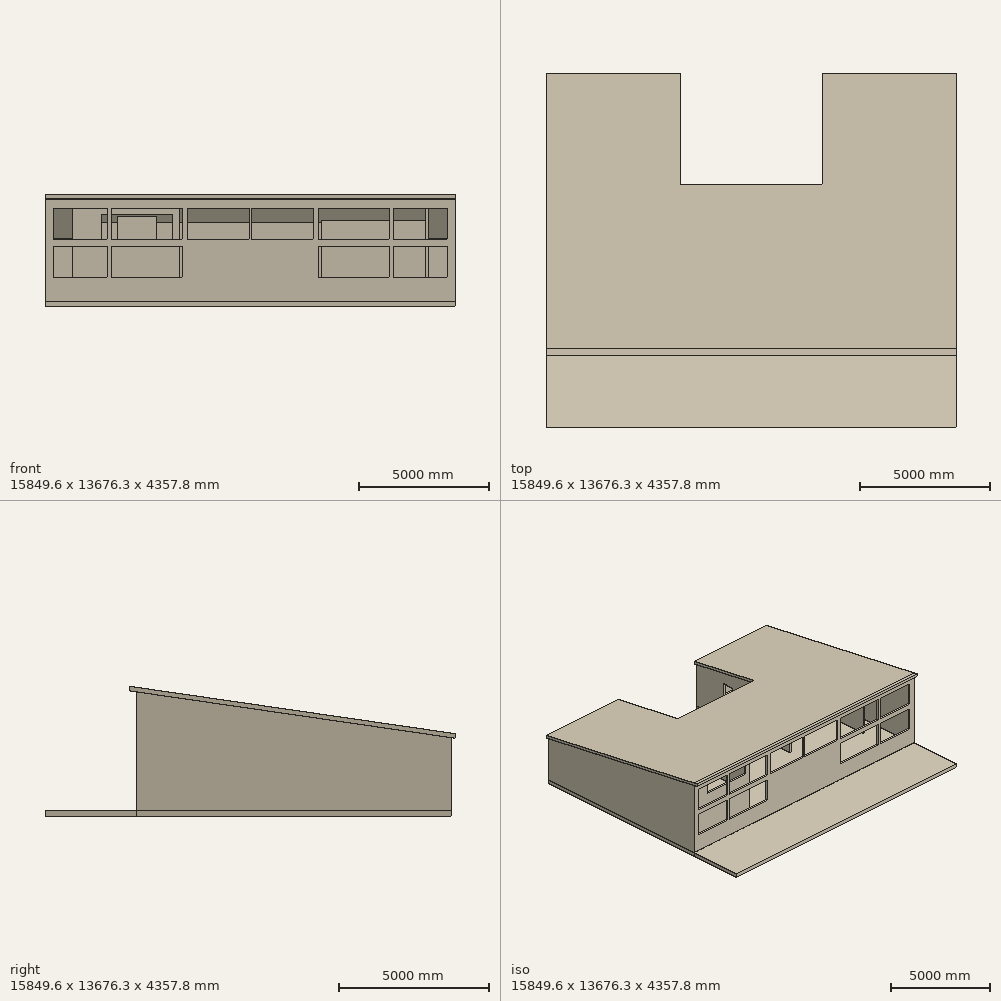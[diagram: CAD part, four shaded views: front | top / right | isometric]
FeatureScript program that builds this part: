
annotation { "Feature Type Name" : "Feature", "Feature Type Description" : "" }
export const myFeature = defineFeature(function(context is Context, id is Id, definition is map)
    precondition{}
    {
        {
            var Q0;
            Q0=qCreatedBy(makeId("Top.planeOp"),FACE);
            var sketch = newSketch(context, id + "F0", { "sketchPlane" : qUnion([Q0])});
            skLineSegment(sketch, "E0", {"start": v(0, 2032) * mm, "end": v(-1523.87, 2032) * mm});
            skLineSegment(sketch, "E1", {"start": v(-2286, 0) * mm, "end": v(-2400.3, 0) * mm});
            skLineSegment(sketch, "E2", {"start": v(-2400.3, 0) * mm, "end": v(-2400.3, 2882.9) * mm});
            skLineSegment(sketch, "E3", {"start": v(-3276.6, 1968.5) * mm, "end": v(-3276.6, -1435.1) * mm});
            skLineSegment(sketch, "E4", {"start": v(-1523.87, 2032) * mm, "end": v(-1523.87, 2235.2) * mm});
            skLineSegment(sketch, "E5", {"start": v(-1473.07, 2286) * mm, "end": v(-50.8, 2286) * mm});
            skLineSegment(sketch, "E6", {"start": v(0, 2235.2) * mm, "end": v(0, 2032) * mm});
            skPoint(sketch, "E7.visualSharp", {"position": v(-1523.87, 2286) * mm});
            skArc(sketch, "E7.filletArc", {"start": v(-1473.07, 2286) * mm, "mid": v(-1509, 2271.12) * mm, "end": v(-1523.87, 2235.2) * mm});
            skPoint(sketch, "E8.visualSharp", {"position": v(0, 2286) * mm});
            skArc(sketch, "E8.filletArc", {"start": v(0, 2235.2) * mm, "mid": v(-14.88, 2271.12) * mm, "end": v(-50.8, 2286) * mm});
            skLineSegment(sketch, "E9", {"start": v(-2286, 0) * mm, "end": v(-2286, 2997.2) * mm});
            skLineSegment(sketch, "E10", {"start": v(-2400.3, 2997.2) * mm, "end": v(-3276.6, 2997.2) * mm});
            skLineSegment(sketch, "E11", {"start": v(-3276.6, 2997.2) * mm, "end": v(-3276.6, 2882.9) * mm});
            skLineSegment(sketch, "E12", {"start": v(-3276.6, 2882.9) * mm, "end": v(-2400.3, 2882.9) * mm});
            skLineSegment(sketch, "E13", {"start": v(-3276.6, 1968.5) * mm, "end": v(-3162.3, 1968.5) * mm});
            skLineSegment(sketch, "E14", {"start": v(-2400.3, 2997.2) * mm, "end": v(-2400.3, 3759.2) * mm});
            skLineSegment(sketch, "E15", {"start": v(-2400.3, 3759.2) * mm, "end": v(-3276.6, 3759.2) * mm});
            skLineSegment(sketch, "E16", {"start": v(-381, 3048) * mm, "end": v(-381, 3771.9) * mm});
            skLineSegment(sketch, "E17", {"start": v(-381, 3048) * mm, "end": v(-266.7, 3048) * mm});
            skLineSegment(sketch, "E18", {"start": v(-266.7, 3048) * mm, "end": v(-266.7, 3657.6) * mm});
            skLineSegment(sketch, "E19", {"start": v(-266.7, 3657.6) * mm, "end": v(762, 3657.6) * mm});
            skLineSegment(sketch, "E20", {"start": v(-381, 3771.9) * mm, "end": v(762, 3771.9) * mm});
            skLineSegment(sketch, "E21", {"start": v(762, 3771.9) * mm, "end": v(762, 5346.7) * mm});
            skLineSegment(sketch, "E22", {"start": v(-1143, 3048) * mm, "end": v(-1257.3, 3048) * mm});
            skLineSegment(sketch, "E23", {"start": v(-1257.3, 3048) * mm, "end": v(-1257.3, 3657.6) * mm});
            skLineSegment(sketch, "E24", {"start": v(-1257.3, 3657.6) * mm, "end": v(-2286, 3657.6) * mm});
            skLineSegment(sketch, "E25", {"start": v(-2286, 3657.6) * mm, "end": v(-2286, 2997.2) * mm});
            skLineSegment(sketch, "E26", {"start": v(-1143, 3048) * mm, "end": v(-1143, 3771.9) * mm});
            skLineSegment(sketch, "E27", {"start": v(-1143, 3771.9) * mm, "end": v(-2286, 3771.9) * mm});
            skLineSegment(sketch, "E28", {"start": v(762, 5346.7) * mm, "end": v(-2286, 5346.7) * mm});
            skLineSegment(sketch, "E29", {"start": v(-3276.6, 3759.2) * mm, "end": v(-3276.6, 3956.05) * mm});
            skLineSegment(sketch, "E30", {"start": v(-3276.6, 3956.05) * mm, "end": v(-3162.3, 3956.05) * mm});
            skLineSegment(sketch, "E31", {"start": v(-3162.3, 3956.05) * mm, "end": v(-3162.3, 3873.5) * mm});
            skLineSegment(sketch, "E32", {"start": v(-3162.3, 3873.5) * mm, "end": v(-2286, 3873.5) * mm});
            skLineSegment(sketch, "E33", {"start": v(-2286, 3873.5) * mm, "end": v(-2286, 3771.9) * mm});
            skLineSegment(sketch, "E34", {"start": v(-3276.6, 4718.05) * mm, "end": v(-3162.3, 4718.05) * mm});
            skLineSegment(sketch, "E35", {"start": v(-3162.3, 4718.05) * mm, "end": v(-3162.3, 4775.2) * mm});
            skLineSegment(sketch, "E36", {"start": v(-3162.3, 4775.2) * mm, "end": v(-2286, 4775.2) * mm});
            skLineSegment(sketch, "E37", {"start": v(-2286, 4775.2) * mm, "end": v(-2286, 5346.7) * mm});
            skLineSegment(sketch, "E38", {"start": v(-3276.6, 4718.05) * mm, "end": v(-3276.6, 4946.65) * mm});
            skLineSegment(sketch, "E39", {"start": v(-3276.6, 4946.65) * mm, "end": v(-3162.3, 4946.65) * mm});
            skLineSegment(sketch, "E40", {"start": v(-3162.3, 4946.65) * mm, "end": v(-3162.3, 4889.5) * mm});
            skLineSegment(sketch, "E41", {"start": v(-3162.3, 4889.5) * mm, "end": v(-2400.3, 4889.5) * mm});
            skLineSegment(sketch, "E42", {"start": v(-2400.3, 4889.5) * mm, "end": v(-2400.3, 6718.3) * mm});
            skLineSegment(sketch, "E43", {"start": v(-2400.3, 6718.3) * mm, "end": v(-3162.3, 6718.3) * mm});
            skLineSegment(sketch, "E44", {"start": v(-3162.3, 6718.3) * mm, "end": v(-3162.3, 6661.15) * mm});
            skLineSegment(sketch, "E45", {"start": v(-3162.3, 6661.15) * mm, "end": v(-3276.6, 6661.15) * mm});
            skLineSegment(sketch, "E46", {"start": v(-3276.6, 6661.15) * mm, "end": v(-3276.6, 6832.6) * mm});
            skLineSegment(sketch, "E47", {"start": v(-3276.6, 6832.6) * mm, "end": v(-2286, 6832.6) * mm});
            skLineSegment(sketch, "E48", {"start": v(-2286, 6832.6) * mm, "end": v(-2286, 5461) * mm});
            skLineSegment(sketch, "E49", {"start": v(-2286, 5461) * mm, "end": v(762, 5461) * mm});
            skLineSegment(sketch, "E50", {"start": v(762, 5461) * mm, "end": v(762, 7747) * mm});
            skLineSegment(sketch, "E51", {"start": v(762, 7747) * mm, "end": v(-4191, 7747) * mm});
            skLineSegment(sketch, "E52", {"start": v(876.3, 7861.3) * mm, "end": v(-4305.3, 7861.3) * mm});
            skLineSegment(sketch, "E53", {"start": v(-4191, 7747) * mm, "end": v(-4191, -2501.9) * mm});
            skLineSegment(sketch, "E54", {"start": v(-4305.3, 7861.3) * mm, "end": v(-4305.3, -2616.2) * mm});
            skLineSegment(sketch, "E55", {"start": v(-4191, -2501.9) * mm, "end": v(876.3, -2501.9) * mm});
            skLineSegment(sketch, "E56", {"start": v(-4305.3, -2616.2) * mm, "end": v(876.3, -2616.2) * mm});
            skLineSegment(sketch, "E57", {"start": v(876.3, -2501.9) * mm, "end": v(6362.7, -2501.9) * mm});
            skLineSegment(sketch, "E58", {"start": v(6362.7, 3708.4) * mm, "end": v(876.3, 3708.4) * mm});
            skLineSegment(sketch, "E59", {"start": v(876.3, -1435.1) * mm, "end": v(876.3, 3594.1) * mm});
            skLineSegment(sketch, "E60", {"start": v(876.3, 7861.3) * mm, "end": v(876.3, 3708.4) * mm});
            skLineSegment(sketch, "E61", {"start": v(876.3, -2616.2) * mm, "end": v(6362.7, -2616.2) * mm});
            skLineSegment(sketch, "E62", {"start": v(6362.7, -2616.2) * mm, "end": v(11544.3, -2616.2) * mm});
            skLineSegment(sketch, "E63", {"start": v(11544.3, -2616.2) * mm, "end": v(11544.3, 7861.3) * mm});
            skLineSegment(sketch, "E64", {"start": v(11544.3, 7861.3) * mm, "end": v(6362.7, 7861.3) * mm});
            skLineSegment(sketch, "E65", {"start": v(6362.7, 7861.3) * mm, "end": v(6362.7, 3708.4) * mm});
            skLineSegment(sketch, "E66", {"start": v(6362.7, -2501.9) * mm, "end": v(11430, -2501.9) * mm});
            skLineSegment(sketch, "E67", {"start": v(11430, -2501.9) * mm, "end": v(11430, 7747) * mm});
            skLineSegment(sketch, "E68", {"start": v(11430, 7747) * mm, "end": v(6477, 7747) * mm});
            skLineSegment(sketch, "E69", {"start": v(10515.6, 6832.6) * mm, "end": v(10401.3, 6832.6) * mm});
            skLineSegment(sketch, "E70", {"start": v(10401.3, 6832.6) * mm, "end": v(10401.3, 4699) * mm});
            skLineSegment(sketch, "E71", {"start": v(10401.3, 4699) * mm, "end": v(9080.5, 4699) * mm});
            skLineSegment(sketch, "E72", {"start": v(9080.5, 4699) * mm, "end": v(9080.5, 5308.6) * mm});
            skLineSegment(sketch, "E73", {"start": v(9080.5, 5308.6) * mm, "end": v(8966.2, 5308.6) * mm});
            skLineSegment(sketch, "E74", {"start": v(8966.2, 5308.6) * mm, "end": v(8966.2, 4699) * mm});
            skLineSegment(sketch, "E75", {"start": v(8966.2, 4699) * mm, "end": v(6477, 4699) * mm});
            skLineSegment(sketch, "E76", {"start": v(6477, 7747) * mm, "end": v(6477, 4699) * mm});
            skLineSegment(sketch, "E77", {"start": v(6477, 4584.7) * mm, "end": v(6477, 3060.7) * mm});
            skLineSegment(sketch, "E78", {"start": v(10515.6, 6832.6) * mm, "end": v(10515.6, 4584.7) * mm});
            skLineSegment(sketch, "E79", {"start": v(6477, 4584.7) * mm, "end": v(9220.2, 4584.7) * mm});
            skLineSegment(sketch, "E80", {"start": v(9220.2, 4584.7) * mm, "end": v(9220.2, 4527.55) * mm});
            skLineSegment(sketch, "E81", {"start": v(9220.2, 4527.55) * mm, "end": v(9334.5, 4527.55) * mm});
            skLineSegment(sketch, "E82", {"start": v(9334.5, 4527.55) * mm, "end": v(9334.5, 4584.7) * mm});
            skLineSegment(sketch, "E83", {"start": v(9334.5, 4584.7) * mm, "end": v(10515.6, 4584.7) * mm});
            skLineSegment(sketch, "E84", {"start": v(6477, 3060.7) * mm, "end": v(9220.2, 3060.7) * mm});
            skLineSegment(sketch, "E85", {"start": v(9220.2, 3060.7) * mm, "end": v(9220.2, 3765.55) * mm});
            skLineSegment(sketch, "E86", {"start": v(9220.2, 3765.55) * mm, "end": v(9334.5, 3765.55) * mm});
            skLineSegment(sketch, "E87", {"start": v(9334.5, 3765.55) * mm, "end": v(9334.5, 3060.7) * mm});
            skLineSegment(sketch, "E88", {"start": v(9334.5, 3060.7) * mm, "end": v(10401.3, 3060.7) * mm});
            skLineSegment(sketch, "E89", {"start": v(876.3, 3594.1) * mm, "end": v(6362.7, 3594.1) * mm});
            skLineSegment(sketch, "E90", {"start": v(10401.3, 3060.7) * mm, "end": v(10401.3, 3670.3) * mm});
            skLineSegment(sketch, "E91", {"start": v(10401.3, 3670.3) * mm, "end": v(10515.6, 3670.3) * mm});
            skLineSegment(sketch, "E92", {"start": v(6477, 2946.4) * mm, "end": v(10401.3, 2946.4) * mm});
            skLineSegment(sketch, "E93", {"start": v(6362.7, 3594.1) * mm, "end": v(6362.7, 1155.7) * mm});
            skLineSegment(sketch, "E94", {"start": v(6362.7, 1155.7) * mm, "end": v(6477, 1155.7) * mm});
            skLineSegment(sketch, "E95", {"start": v(6477, 1155.7) * mm, "end": v(6477, 2946.4) * mm});
            skLineSegment(sketch, "E96", {"start": v(10401.3, 2946.4) * mm, "end": v(10401.3, -101.6) * mm});
            skLineSegment(sketch, "E97", {"start": v(10401.3, -101.6) * mm, "end": v(10515.6, -101.6) * mm});
            skLineSegment(sketch, "E98", {"start": v(10515.6, 3670.3) * mm, "end": v(10515.6, -101.6) * mm});
            skLineSegment(sketch, "E99", {"start": v(-3162.3, 1968.5) * mm, "end": v(-3162.3, -1320.8) * mm});
            skLineSegment(sketch, "E100", {"start": v(876.3, -1435.1) * mm, "end": v(-3276.6, -1435.1) * mm});
            skLineSegment(sketch, "E101", {"start": v(-3162.3, -1320.8) * mm, "end": v(762, -1320.8) * mm});
            skLineSegment(sketch, "E102", {"start": v(762, 3657.6) * mm, "end": v(762, -1320.8) * mm});
            skLineSegment(sketch, "E103", {"start": v(-266.7, 3048) * mm, "end": v(-266.7, 2286) * mm});
            skLineSegment(sketch, "E104", {"start": v(-1257.3, 3048) * mm, "end": v(-1257.3, 2286) * mm});
            skLineSegment(sketch, "E105", {"start": v(-1143, 3048) * mm, "end": v(-381, 3048) * mm});
            skLineSegment(sketch, "E106", {"start": v(-381, 3352.8) * mm, "end": v(-1143, 3352.8) * mm});
            skPoint(sketch, "E106.endSnap0", {"position": v(-1143, 3409.95) * mm});
            skLineSegment(sketch, "E107", {"start": v(-1523.87, 2032) * mm, "end": v(-2286, 2032) * mm});
            skLineSegment(sketch, "E108", {"start": v(0, 2032) * mm, "end": v(762, 2032) * mm});
            skLineSegment(sketch, "E109", {"start": v(-1523.87, 2336.8) * mm, "end": v(-2286, 2336.8) * mm});
            skPoint(sketch, "E110.visualSharp", {"position": v(-1473.2, 2336.8) * mm});
            skArc(sketch, "E110.filletArc", {"start": v(-1473.07, 2286) * mm, "mid": v(-1487.95, 2321.92) * mm, "end": v(-1523.87, 2336.8) * mm});
            skLineSegment(sketch, "E111", {"start": v(-50.8, 2286) * mm, "end": v(-50.8, 2286) * mm});
            skLineSegment(sketch, "E112", {"start": v(0, 2336.8) * mm, "end": v(762, 2336.8) * mm});
            skPoint(sketch, "E113.visualSharp", {"position": v(-50.8, 2336.8) * mm});
            skArc(sketch, "E113.filletArc", {"start": v(0, 2336.8) * mm, "mid": v(-35.92, 2321.92) * mm, "end": v(-50.8, 2286) * mm});
            skLineSegment(sketch, "E114", {"start": v(-2400.3, 0) * mm, "end": v(-3162.3, 0) * mm});
            skLineSegment(sketch, "E115", {"start": v(-3162.3, 457.2) * mm, "end": v(-2400.3, 457.2) * mm});
            skLineSegment(sketch, "E116", {"start": v(-3162.3, 914.4) * mm, "end": v(-2400.3, 914.4) * mm});
            skLineSegment(sketch, "E117", {"start": v(-3162.3, 1371.6) * mm, "end": v(-2400.3, 1371.6) * mm});
            skLineSegment(sketch, "E118", {"start": v(-3162.3, 1828.8) * mm, "end": v(-2400.3, 1828.8) * mm});
            skSolve(sketch);
        }
        {
            var Q0;
            {var subQ0=sQuery(id+"F0.wireOp",EDGE,"E105");Q0=makeQuery(id+"F0.imprint","IMPRINT",FACE,{"disambiguationData":[TD([[makeQuery(id+"F0.imprint","IMPRINT",EDGE,{"derivedFrom":subQ0}),1.0]])]});}
            var Q1;
            {var subQ0=sQuery(id+"F0.wireOp",EDGE,"E117");Q1=makeQuery(id+"F0.imprint","IMPRINT",FACE,{"disambiguationData":[TD([[makeQuery(id+"F0.imprint","IMPRINT",EDGE,{"derivedFrom":subQ0}),1.0]])]});}
            extrude(context, id + "F1", {"entities" : qUnion([Q0, Q1]), "depth" : 203.2 * mm, "offsetDistance" : 25.4 * mm});
        }
        {
            var Q0;
            Q0=makeQuery(id+"F0.imprint","IMPRINT",FACE,{"disambiguationData":[TD([[makeQuery(id+"F0.imprint","IMPRINT",EDGE,{"derivedFrom":sQuery(id+"F0.wireOp",EDGE,"E17")}),-1.0]])]});
            var Q1;
            {var subQ0=sQuery(id+"F0.wireOp",EDGE,"E116");Q1=makeQuery(id+"F0.imprint","IMPRINT",FACE,{"disambiguationData":[TD([[makeQuery(id+"F0.imprint","IMPRINT",EDGE,{"derivedFrom":subQ0}),1.0]])]});}
            extrude(context, id + "F2", {"entities" : qUnion([Q0, Q1]), "depth" : 406.4 * mm, "offsetDistance" : 25.4 * mm});
        }
        {
            var Q0;
            Q0=makeQuery(id+"F0.imprint","IMPRINT",FACE,{"disambiguationData":[TD([[makeQuery(id+"F0.imprint","IMPRINT",EDGE,{"derivedFrom":sQuery(id+"F0.wireOp",EDGE,"E23")}),1.0]])]});
            var Q1;
            Q1=makeQuery(id+"F0.imprint","IMPRINT",FACE,{"disambiguationData":[TD([[makeQuery(id+"F0.imprint","IMPRINT",EDGE,{"derivedFrom":sQuery(id+"F0.wireOp",EDGE,"E18")}),-1.0]])]});
            var Q2;
            {var subQ0=sQuery(id+"F0.wireOp",EDGE,"E115");Q2=makeQuery(id+"F0.imprint","IMPRINT",FACE,{"disambiguationData":[TD([[makeQuery(id+"F0.imprint","IMPRINT",EDGE,{"derivedFrom":subQ0}),1.0]])]});}
            extrude(context, id + "F3", {"entities" : qUnion([Q0, Q1, Q2]), "depth" : 609.6 * mm, "offsetDistance" : 25.4 * mm});
        }
        {
            var Q0;
            Q0=makeQuery(id+"F0.imprint","IMPRINT",FACE,{"disambiguationData":[TD([[makeQuery(id+"F0.imprint","IMPRINT",EDGE,{"derivedFrom":sQuery(id+"F0.wireOp",EDGE,"E4")}),1.0]])]});
            var Q1;
            Q1=makeQuery(id+"F0.imprint","IMPRINT",FACE,{"disambiguationData":[TD([[makeQuery(id+"F0.imprint","IMPRINT",EDGE,{"derivedFrom":sQuery(id+"F0.wireOp",EDGE,"E6")}),1.0]])]});
            var Q2;
            {var subQ0=sQuery(id+"F0.wireOp",EDGE,"E114");Q2=makeQuery(id+"F0.imprint","IMPRINT",FACE,{"disambiguationData":[TD([[makeQuery(id+"F0.imprint","IMPRINT",EDGE,{"derivedFrom":subQ0}),-1.0]])]});}
            extrude(context, id + "F4", {"entities" : qUnion([Q0, Q1, Q2]), "depth" : 812.8 * mm, "offsetDistance" : 25.4 * mm});
        }
        {
            var Q0;
            Q0=makeQuery(id+"F0.imprint","IMPRINT",FACE,{"disambiguationData":[TD([[makeQuery(id+"F0.imprint","IMPRINT",EDGE,{"derivedFrom":sQuery(id+"F0.wireOp",EDGE,"E0")}),1.0]])]});
            extrude(context, id + "F5", {"entities" : qUnion([Q0]), "depth" : 1016 * mm, "offsetDistance" : 25.4 * mm});
        }
        {
            var Q0;
            Q0=qCreatedBy(makeId("Right.planeOp"),FACE);
            var sketch = newSketch(context, id + "F6", { "sketchPlane" : qUnion([Q0])});
            skLineSegment(sketch, "E119", {"start": v(0, 0) * mm, "end": v(-2616.2, 0) * mm, "construction": true});
            skLineSegment(sketch, "E120", {"start": v(-2616.2, 0) * mm, "end": v(-2616.2, 3962.4) * mm, "construction": true});
            skLineSegment(sketch, "E121", {"start": v(0, 0) * mm, "end": v(7861.3, 0) * mm, "construction": true});
            skLineSegment(sketch, "E122", {"start": v(7861.3, 0) * mm, "end": v(7861.3, 2438.4) * mm, "construction": true});
            skLineSegment(sketch, "E123", {"start": v(7861.3, 2438.4) * mm, "end": v(-2616.2, 3962.4) * mm});
            skLineSegment(sketch, "E124", {"start": v(7861.3, 2438.4) * mm, "end": v(7861.3, 2590.8) * mm});
            skLineSegment(sketch, "E125", {"start": v(7861.3, 2590.8) * mm, "end": v(-2616.2, 4114.8) * mm});
            skLineSegment(sketch, "E126", {"start": v(-2616.2, 4114.8) * mm, "end": v(-2616.2, 3962.4) * mm});
            skLineSegment(sketch, "E127", {"start": v(-2616.2, 3962.4) * mm, "end": v(-2867.55, 3998.96) * mm});
            skLineSegment(sketch, "E128", {"start": v(-2616.2, 4114.8) * mm, "end": v(-2867.55, 4154.56) * mm});
            skLineSegment(sketch, "E129", {"start": v(-2867.55, 4154.56) * mm, "end": v(-2867.55, 3998.96) * mm});
            skLineSegment(sketch, "E130", {"start": v(7861.3, 2438.4) * mm, "end": v(8012.11, 2416.46) * mm});
            skLineSegment(sketch, "E131", {"start": v(7861.3, 2590.8) * mm, "end": v(8012.11, 2568.86) * mm});
            skLineSegment(sketch, "E132", {"start": v(8012.11, 2568.86) * mm, "end": v(8012.11, 2416.46) * mm});
            skSolve(sketch);
        }
        {
            var Q0;
            Q0=makeQuery(id+"F6.imprint","IMPRINT",FACE,{"disambiguationData":[TD([[makeQuery(id+"F6.imprint","IMPRINT",EDGE,{"derivedFrom":sQuery(id+"F6.wireOp",EDGE,"E123")}),-1.0]])]});
            var Q1;
            Q1=makeQuery(id+"F6.imprint","IMPRINT",FACE,{"disambiguationData":[TD([[makeQuery(id+"F6.imprint","IMPRINT",EDGE,{"derivedFrom":sQuery(id+"F6.wireOp",EDGE,"E126")}),-1.0]])]});
            var Q2;
            Q2=makeQuery(id+"F6.imprint","IMPRINT",FACE,{"disambiguationData":[TD([[makeQuery(id+"F6.imprint","IMPRINT",EDGE,{"derivedFrom":sQuery(id+"F6.wireOp",EDGE,"E124")}),-1.0]])]});
            var Q3;
            Q3=sQuery(id+"F0.wireOp",VERTEX,"E63.end");
            var Q4;
            Q4=sQuery(id+"F0.wireOp",VERTEX,"E54.end");
            extrude(context, id + "F7", {"entities" : qUnion([Q0, Q1, Q2]), "endBound" : BoundingType.UP_TO_VERTEX, "depth" : 25.4 * mm, "endBoundEntityVertex" : qUnion([Q3]), "offsetDistance" : 25.4 * mm, "hasSecondDirection" : true, "secondDirectionBound" : BoundingType.UP_TO_VERTEX, "secondDirectionOppositeDirection" : true, "secondDirectionDepth" : 25.4 * mm, "secondDirectionBoundEntityVertex" : qUnion([Q4])});
        }
        {
            var Q0;
            Q0=makeQuery(id+"F0.imprint","IMPRINT",FACE,{"disambiguationData":[TD([[makeQuery(id+"F0.imprint","IMPRINT",EDGE,{"derivedFrom":sQuery(id+"F0.wireOp",EDGE,"E0")}),-1.0]])]});
            var Q1;
            Q1=makeQuery(id+"F0.imprint","IMPRINT",FACE,{"disambiguationData":[TD([[makeQuery(id+"F0.imprint","IMPRINT",EDGE,{"derivedFrom":sQuery(id+"F0.wireOp",EDGE,"E1")}),-1.0]])]});
            var Q2;
            Q2=makeQuery(id+"F0.imprint","IMPRINT",FACE,{"disambiguationData":[TD([[makeQuery(id+"F0.imprint","IMPRINT",EDGE,{"derivedFrom":sQuery(id+"F0.wireOp",EDGE,"E3")}),1.0]])]});
            var Q3;
            Q3=makeQuery(id+"F7.opExtrude","SWEPT_FACE",FACE,{"disambiguationData":[OSD([sQuery(id+"F6.wireOp",EDGE,"E123"),sQuery(id+"F6.wireOp",EDGE,"E127"),sQuery(id+"F6.wireOp",EDGE,"E130")])]});
            extrude(context, id + "F8", {"entities" : qUnion([Q0, Q1, Q2]), "endBound" : BoundingType.UP_TO_SURFACE, "depth" : 4267.2 * mm, "endBoundEntityFace" : qUnion([Q3]), "offsetDistance" : 25.4 * mm});
        }
        {
            var Q0;
            Q0=makeQuery(id+"F7.opExtrude","SWEPT_FACE",FACE,{"disambiguationData":[OSD([sQuery(id+"F6.wireOp",EDGE,"E123"),sQuery(id+"F6.wireOp",EDGE,"E127"),sQuery(id+"F6.wireOp",EDGE,"E130")])]});
            var sketch = newSketch(context, id + "F9", { "sketchPlane" : qUnion([Q0])});
            skLineSegment(sketch, "E133.0.0", {"start": v(6362.7, -3669.78) * mm, "end": v(6362.7, -3231.85) * mm});
            skLineSegment(sketch, "E133.0.1", {"start": v(6362.7, -3231.85) * mm, "end": v(6362.7, -7428.45) * mm});
            skLineSegment(sketch, "E133.0.2", {"start": v(6362.7, -7428.45) * mm, "end": v(6362.7, -7779.44) * mm});
            skLineSegment(sketch, "E133.0.3", {"start": v(6362.7, -7779.44) * mm, "end": v(6362.7, -3669.78) * mm});
            skLineSegment(sketch, "E134.0.0", {"start": v(876.3, -3669.78) * mm, "end": v(876.3, -3231.85) * mm});
            skLineSegment(sketch, "E134.0.1", {"start": v(876.3, -3231.85) * mm, "end": v(6362.7, -3231.85) * mm});
            skLineSegment(sketch, "E134.0.2", {"start": v(6362.7, -3231.85) * mm, "end": v(6362.7, -3669.78) * mm});
            skLineSegment(sketch, "E134.0.3", {"start": v(6362.7, -3669.78) * mm, "end": v(876.3, -3669.78) * mm});
            skLineSegment(sketch, "E135.0.0", {"start": v(876.3, -7428.45) * mm, "end": v(876.3, -3231.85) * mm});
            skLineSegment(sketch, "E135.0.1", {"start": v(876.3, -3231.85) * mm, "end": v(876.3, -3669.78) * mm});
            skLineSegment(sketch, "E135.0.2", {"start": v(876.3, -3669.78) * mm, "end": v(876.3, -7779.44) * mm});
            skLineSegment(sketch, "E135.0.3", {"start": v(876.3, -7779.44) * mm, "end": v(876.3, -7428.45) * mm});
            skSolve(sketch);
        }
        {
            var Q0;
            {var subQ0=sQuery(id+"F9.wireOp",EDGE,"E134.0.3");Q0=makeQuery(id+"F9.imprint","IMPRINT",FACE,{"disambiguationData":[TD([[makeQuery(id+"F9.imprint","IMPRINT",EDGE,{"derivedFrom":subQ0}),1.0]])]});}
            var Q1;
            Q1=makeQuery(id+"F9.imprint","IMPRINT",FACE,{"disambiguationData":[TD([[makeQuery(id+"F9.imprint","IMPRINT",EDGE,{"derivedFrom":sQuery(id+"F9.wireOp",EDGE,"E134.0.1")}),-1.0]])]});
            extrude(context, id + "F10", {"entities" : qUnion([Q0, Q1]), "operationType" : NewBodyOperationType.REMOVE, "oppositeDirection" : true, "depth" : 152.4 * mm, "offsetDistance" : 25.4 * mm});
        }
        {
            var Q0;
            Q0=makeQuery(id+"F8.opExtrude","SWEPT_FACE",FACE,{"disambiguationData":[OSD([sQuery(id+"F0.wireOp",EDGE,"E56"),sQuery(id+"F0.wireOp",EDGE,"E61"),sQuery(id+"F0.wireOp",EDGE,"E62")])]});
            var sketch = newSketch(context, id + "F11", { "sketchPlane" : qUnion([Q0])});
            skLineSegment(sketch, "E136.0.0", {"start": v(11544.3, 0) * mm, "end": v(11544.3, 3962.4) * mm});
            skLineSegment(sketch, "E136.0.1", {"start": v(11544.3, 3962.4) * mm, "end": v(-4305.3, 3962.4) * mm});
            skLineSegment(sketch, "E136.0.2", {"start": v(-4305.3, 3962.4) * mm, "end": v(-4305.3, 0) * mm});
            skLineSegment(sketch, "E136.0.3", {"start": v(-4305.3, 0) * mm, "end": v(11544.3, 0) * mm});
            skLineSegment(sketch, "E137", {"start": v(3619.5, 0) * mm, "end": v(6057.9, 0) * mm});
            skLineSegment(sketch, "E138", {"start": v(3619.5, 0) * mm, "end": v(1181.1, 0) * mm});
            skLineSegment(sketch, "E139", {"start": v(6057.9, 0) * mm, "end": v(6057.9, 2057.4) * mm});
            skLineSegment(sketch, "E140", {"start": v(6057.9, 2057.4) * mm, "end": v(1181.1, 2057.4) * mm});
            skLineSegment(sketch, "E141", {"start": v(1181.1, 2057.4) * mm, "end": v(1181.1, 0) * mm});
            skLineSegment(sketch, "E142", {"start": v(1181.1, 1028.7) * mm, "end": v(977.9, 1028.7) * mm, "construction": true});
            skLineSegment(sketch, "E143", {"start": v(977.9, 0) * mm, "end": v(977.9, 914.4) * mm, "construction": true});
            skLineSegment(sketch, "E144", {"start": v(977.9, 914.4) * mm, "end": v(977.9, 2133.6) * mm});
            skLineSegment(sketch, "E145", {"start": v(977.9, 2133.6) * mm, "end": v(-1739.9, 2133.6) * mm});
            skLineSegment(sketch, "E146", {"start": v(977.9, 914.4) * mm, "end": v(-1739.9, 914.4) * mm});
            skLineSegment(sketch, "E147", {"start": v(-1739.9, 914.4) * mm, "end": v(-1739.9, 2133.6) * mm});
            skLineSegment(sketch, "E148", {"start": v(-1739.9, 914.4) * mm, "end": v(-1892.3, 914.4) * mm, "construction": true});
            skLineSegment(sketch, "E149", {"start": v(-1892.3, 914.4) * mm, "end": v(-1892.3, 2133.6) * mm});
            skLineSegment(sketch, "E150", {"start": v(-1892.3, 2133.6) * mm, "end": v(-4000.5, 2133.6) * mm});
            skLineSegment(sketch, "E151", {"start": v(-1892.3, 914.4) * mm, "end": v(-4000.5, 914.4) * mm});
            skLineSegment(sketch, "E152", {"start": v(-4000.5, 914.4) * mm, "end": v(-4000.5, 2133.6) * mm});
            skLineSegment(sketch, "E153", {"start": v(6057.9, 1028.7) * mm, "end": v(6261.1, 1028.7) * mm, "construction": true});
            skLineSegment(sketch, "E154", {"start": v(6261.1, 0) * mm, "end": v(6261.1, 914.4) * mm, "construction": true});
            skLineSegment(sketch, "E155", {"start": v(6261.1, 914.4) * mm, "end": v(6261.1, 2133.6) * mm});
            skLineSegment(sketch, "E156", {"start": v(6261.1, 2133.6) * mm, "end": v(8978.9, 2133.6) * mm});
            skLineSegment(sketch, "E157", {"start": v(6261.1, 914.4) * mm, "end": v(8978.9, 914.4) * mm});
            skLineSegment(sketch, "E158", {"start": v(8978.9, 914.4) * mm, "end": v(8978.9, 2133.6) * mm});
            skLineSegment(sketch, "E159", {"start": v(8978.9, 914.4) * mm, "end": v(9131.3, 914.4) * mm, "construction": true});
            skLineSegment(sketch, "E160", {"start": v(9131.3, 914.4) * mm, "end": v(9131.3, 2133.6) * mm});
            skLineSegment(sketch, "E161", {"start": v(9131.3, 2133.6) * mm, "end": v(11239.5, 2133.6) * mm});
            skLineSegment(sketch, "E162", {"start": v(11239.5, 2133.6) * mm, "end": v(11239.5, 914.4) * mm});
            skLineSegment(sketch, "E163", {"start": v(11239.5, 914.4) * mm, "end": v(9131.3, 914.4) * mm});
            skLineSegment(sketch, "E164", {"start": v(977.9, 2133.6) * mm, "end": v(977.9, 2387.6) * mm, "construction": true});
            skLineSegment(sketch, "E165", {"start": v(977.9, 2387.6) * mm, "end": v(-1739.9, 2387.6) * mm});
            skLineSegment(sketch, "E166", {"start": v(977.9, 2387.6) * mm, "end": v(977.9, 3606.8) * mm});
            skLineSegment(sketch, "E167", {"start": v(-1739.9, 2387.6) * mm, "end": v(-1739.9, 3606.8) * mm});
            skLineSegment(sketch, "E168", {"start": v(-1739.9, 3606.8) * mm, "end": v(977.9, 3606.8) * mm});
            skLineSegment(sketch, "E169", {"start": v(-1892.3, 2387.6) * mm, "end": v(-4000.5, 2387.6) * mm});
            skLineSegment(sketch, "E170", {"start": v(-4000.5, 2387.6) * mm, "end": v(-4000.5, 3606.8) * mm});
            skLineSegment(sketch, "E171", {"start": v(-4000.5, 3606.8) * mm, "end": v(-1892.3, 3606.8) * mm});
            skLineSegment(sketch, "E172", {"start": v(-1892.3, 3606.8) * mm, "end": v(-1892.3, 2387.6) * mm});
            skLineSegment(sketch, "E173", {"start": v(6261.1, 2387.6) * mm, "end": v(6261.1, 3606.8) * mm});
            skLineSegment(sketch, "E174", {"start": v(6261.1, 3606.8) * mm, "end": v(8978.9, 3606.8) * mm});
            skLineSegment(sketch, "E175", {"start": v(8978.9, 3606.8) * mm, "end": v(8978.9, 2387.6) * mm});
            skLineSegment(sketch, "E176", {"start": v(8978.9, 2387.6) * mm, "end": v(6261.1, 2387.6) * mm});
            skLineSegment(sketch, "E177", {"start": v(9131.3, 2387.6) * mm, "end": v(9131.3, 3606.8) * mm});
            skLineSegment(sketch, "E178", {"start": v(9131.3, 2387.6) * mm, "end": v(11239.5, 2387.6) * mm});
            skLineSegment(sketch, "E179", {"start": v(11239.5, 2387.6) * mm, "end": v(11239.5, 3606.8) * mm});
            skLineSegment(sketch, "E180", {"start": v(11239.5, 3606.8) * mm, "end": v(9131.3, 3606.8) * mm});
            skLineSegment(sketch, "E181", {"start": v(1181.1, 2387.6) * mm, "end": v(3594.1, 2387.6) * mm});
            skLineSegment(sketch, "E182", {"start": v(3594.1, 2387.6) * mm, "end": v(3594.1, 3606.8) * mm});
            skLineSegment(sketch, "E183", {"start": v(3594.1, 3606.8) * mm, "end": v(1181.1, 3606.8) * mm});
            skLineSegment(sketch, "E184", {"start": v(1181.1, 3606.8) * mm, "end": v(1181.1, 2387.6) * mm});
            skLineSegment(sketch, "E185", {"start": v(6057.9, 2387.6) * mm, "end": v(6057.9, 3606.8) * mm});
            skLineSegment(sketch, "E186", {"start": v(6057.9, 3606.8) * mm, "end": v(3644.9, 3606.8) * mm});
            skLineSegment(sketch, "E187", {"start": v(6057.9, 2387.6) * mm, "end": v(3644.9, 2387.6) * mm});
            skLineSegment(sketch, "E188", {"start": v(3644.9, 2387.6) * mm, "end": v(3644.9, 3606.8) * mm});
            skSolve(sketch);
        }
        {
            var Q0;
            Q0=makeQuery(id+"F11.imprint","IMPRINT",FACE,{"disambiguationData":[TD([[makeQuery(id+"F11.imprint","IMPRINT",EDGE,{"derivedFrom":sQuery(id+"F11.wireOp",EDGE,"E149")}),1.0]])]});
            var Q1;
            Q1=makeQuery(id+"F11.imprint","IMPRINT",FACE,{"disambiguationData":[TD([[makeQuery(id+"F11.imprint","IMPRINT",EDGE,{"derivedFrom":sQuery(id+"F11.wireOp",EDGE,"E144")}),1.0]])]});
            var Q2;
            Q2=makeQuery(id+"F11.imprint","IMPRINT",FACE,{"disambiguationData":[TD([[makeQuery(id+"F11.imprint","IMPRINT",EDGE,{"derivedFrom":sQuery(id+"F11.wireOp",EDGE,"E137")}),1.0]])]});
            var Q3;
            Q3=makeQuery(id+"F11.imprint","IMPRINT",FACE,{"disambiguationData":[TD([[makeQuery(id+"F11.imprint","IMPRINT",EDGE,{"derivedFrom":sQuery(id+"F11.wireOp",EDGE,"E155")}),-1.0]])]});
            var Q4;
            Q4=makeQuery(id+"F11.imprint","IMPRINT",FACE,{"disambiguationData":[TD([[makeQuery(id+"F11.imprint","IMPRINT",EDGE,{"derivedFrom":sQuery(id+"F11.wireOp",EDGE,"E160")}),-1.0]])]});
            var Q5;
            Q5=makeQuery(id+"F11.imprint","IMPRINT",FACE,{"disambiguationData":[TD([[makeQuery(id+"F11.imprint","IMPRINT",EDGE,{"derivedFrom":sQuery(id+"F11.wireOp",EDGE,"E173")}),-1.0]])]});
            var Q6;
            Q6=makeQuery(id+"F11.imprint","IMPRINT",FACE,{"disambiguationData":[TD([[makeQuery(id+"F11.imprint","IMPRINT",EDGE,{"derivedFrom":sQuery(id+"F11.wireOp",EDGE,"E177")}),-1.0]])]});
            var Q7;
            Q7=makeQuery(id+"F11.imprint","IMPRINT",FACE,{"disambiguationData":[TD([[makeQuery(id+"F11.imprint","IMPRINT",EDGE,{"derivedFrom":sQuery(id+"F11.wireOp",EDGE,"E165")}),-1.0]])]});
            var Q8;
            Q8=makeQuery(id+"F11.imprint","IMPRINT",FACE,{"disambiguationData":[TD([[makeQuery(id+"F11.imprint","IMPRINT",EDGE,{"derivedFrom":sQuery(id+"F11.wireOp",EDGE,"E169")}),-1.0]])]});
            var Q9;
            Q9=makeQuery(id+"F11.imprint","IMPRINT",FACE,{"disambiguationData":[TD([[makeQuery(id+"F11.imprint","IMPRINT",EDGE,{"derivedFrom":sQuery(id+"F11.wireOp",EDGE,"E181")}),1.0]])]});
            var Q10;
            Q10=makeQuery(id+"F11.imprint","IMPRINT",FACE,{"disambiguationData":[TD([[makeQuery(id+"F11.imprint","IMPRINT",EDGE,{"derivedFrom":sQuery(id+"F11.wireOp",EDGE,"E185")}),1.0]])]});
            extrude(context, id + "F12", {"entities" : qUnion([Q0, Q1, Q2, Q3, Q4, Q5, Q6, Q7, Q8, Q9, Q10]), "operationType" : NewBodyOperationType.REMOVE, "oppositeDirection" : true, "depth" : 114.3 * mm, "offsetDistance" : 25.4 * mm});
        }
        {
            var Q0;
            Q0=makeQuery(id+"F8.opExtrude","SWEPT_FACE",FACE,{"disambiguationData":[OSD([sQuery(id+"F0.wireOp",EDGE,"E65")])]});
            var sketch = newSketch(context, id + "F13", { "sketchPlane" : qUnion([Q0])});
            skLineSegment(sketch, "E189", {"start": v(-7861.3, 0) * mm, "end": v(-7861.3, 914.4) * mm, "construction": true});
            skLineSegment(sketch, "E190", {"start": v(-7861.3, 914.4) * mm, "end": v(-5308.6, 871.53) * mm, "construction": true});
            skLineSegment(sketch, "E191", {"start": v(-5308.6, 871.53) * mm, "end": v(-5288.02, 2096.9) * mm});
            skLineSegment(sketch, "E192", {"start": v(-5288.02, 2096.9) * mm, "end": v(-5913.4, 2107.41) * mm});
            skLineSegment(sketch, "E193", {"start": v(-5913.4, 2107.41) * mm, "end": v(-5934.16, 871.53) * mm});
            skLineSegment(sketch, "E194", {"start": v(-5934.16, 871.53) * mm, "end": v(-5308.6, 871.53) * mm});
            skSolve(sketch);
        }
        {
            var Q0;
            Q0=makeQuery(id+"F13.imprint","IMPRINT",FACE,{"disambiguationData":[TD([[makeQuery(id+"F13.imprint","IMPRINT",EDGE,{"derivedFrom":sQuery(id+"F13.wireOp",EDGE,"E191")}),1.0]])]});
            extrude(context, id + "F14", {"entities" : qUnion([Q0]), "operationType" : NewBodyOperationType.REMOVE, "oppositeDirection" : true, "depth" : 114.3 * mm, "offsetDistance" : 25.4 * mm});
        }
        {
            var Q0;
            Q0=makeQuery(id+"F8.opExtrude","SWEPT_FACE",FACE,{"disambiguationData":[OSD([sQuery(id+"F0.wireOp",EDGE,"E58")])]});
            var sketch = newSketch(context, id + "F15", { "sketchPlane" : qUnion([Q0])});
            skLineSegment(sketch, "E195", {"start": v(-876.3, 0) * mm, "end": v(-1181.1, 0) * mm, "construction": true});
            skLineSegment(sketch, "E196", {"start": v(-1181.1, 0) * mm, "end": v(-1181.1, 2082.8) * mm});
            skLineSegment(sketch, "E197", {"start": v(-1181.1, 2082.8) * mm, "end": v(-2882.9, 2082.8) * mm});
            skLineSegment(sketch, "E198", {"start": v(-2882.9, 2082.8) * mm, "end": v(-2882.9, 0) * mm});
            skLineSegment(sketch, "E199", {"start": v(-2882.9, 0) * mm, "end": v(-1181.1, 0) * mm});
            skLineSegment(sketch, "E200", {"start": v(-2882.9, 0) * mm, "end": v(-3492.5, 0) * mm, "construction": true});
            skLineSegment(sketch, "E201", {"start": v(-3492.5, 0) * mm, "end": v(-3492.5, 914.4) * mm, "construction": true});
            skLineSegment(sketch, "E202", {"start": v(-3492.5, 914.4) * mm, "end": v(-3492.5, 1838.33) * mm});
            skLineSegment(sketch, "E203", {"start": v(-3492.5, 1838.33) * mm, "end": v(-5718.18, 1838.33) * mm});
            skLineSegment(sketch, "E204", {"start": v(-5718.18, 1838.33) * mm, "end": v(-5718.18, 914.4) * mm});
            skLineSegment(sketch, "E205", {"start": v(-5718.18, 914.4) * mm, "end": v(-3492.5, 914.4) * mm});
            skSolve(sketch);
        }
        {
            var Q0;
            Q0=makeQuery(id+"F15.imprint","IMPRINT",FACE,{"disambiguationData":[TD([[makeQuery(id+"F15.imprint","IMPRINT",EDGE,{"derivedFrom":sQuery(id+"F15.wireOp",EDGE,"E202")}),1.0]])]});
            var Q1;
            Q1=makeQuery(id+"F15.imprint","IMPRINT",FACE,{"disambiguationData":[TD([[makeQuery(id+"F15.imprint","IMPRINT",EDGE,{"derivedFrom":sQuery(id+"F15.wireOp",EDGE,"E196")}),1.0]])]});
            extrude(context, id + "F16", {"entities" : qUnion([Q0, Q1]), "operationType" : NewBodyOperationType.REMOVE, "oppositeDirection" : true, "depth" : 114.3 * mm, "offsetDistance" : 25.4 * mm});
        }
        {
            var Q0;
            Q0=makeQuery(id+"F8.opExtrude","SWEPT_FACE",FACE,{"disambiguationData":[OSD([sQuery(id+"F0.wireOp",EDGE,"E60")])]});
            var sketch = newSketch(context, id + "F17", { "sketchPlane" : qUnion([Q0])});
            skLineSegment(sketch, "E206", {"start": v(7861.3, 0) * mm, "end": v(7251.7, 0) * mm, "construction": true});
            skLineSegment(sketch, "E207", {"start": v(7251.7, 0) * mm, "end": v(7251.7, 914.4) * mm, "construction": true});
            skLineSegment(sketch, "E208", {"start": v(7251.7, 914.4) * mm, "end": v(7251.7, 2139.95) * mm});
            skLineSegment(sketch, "E209", {"start": v(7251.7, 2139.95) * mm, "end": v(6026.15, 2139.95) * mm});
            skLineSegment(sketch, "E210", {"start": v(7251.7, 914.4) * mm, "end": v(6026.15, 914.4) * mm});
            skLineSegment(sketch, "E211", {"start": v(6026.15, 914.4) * mm, "end": v(6026.15, 2139.95) * mm});
            skSolve(sketch);
        }
        {
            var Q0;
            Q0=makeQuery(id+"F17.imprint","IMPRINT",FACE,{"disambiguationData":[TD([[makeQuery(id+"F17.imprint","IMPRINT",EDGE,{"derivedFrom":sQuery(id+"F17.wireOp",EDGE,"E208")}),1.0]])]});
            extrude(context, id + "F18", {"entities" : qUnion([Q0]), "operationType" : NewBodyOperationType.REMOVE, "oppositeDirection" : true, "depth" : 114.3 * mm, "offsetDistance" : 25.4 * mm});
        }
        {
            var Q0;
            Q0=makeQuery(id+"F8.opExtrude","SWEPT_FACE",FACE,{"disambiguationData":[OSD([sQuery(id+"F0.wireOp",EDGE,"E100")])]});
            var sketch = newSketch(context, id + "F19", { "sketchPlane" : qUnion([Q0])});
            skLineSegment(sketch, "E212.0", {"start": v(-3162.3, 1016) * mm, "end": v(762, 1016) * mm, "construction": true});
            skLineSegment(sketch, "E213.0", {"start": v(762, 3773.98) * mm, "end": v(762, 0) * mm, "construction": true});
            skLineSegment(sketch, "E214", {"start": v(-1200.15, 1016) * mm, "end": v(-1200.15, 2133.6) * mm, "construction": true});
            skLineSegment(sketch, "E215.0", {"start": v(876.3, 0) * mm, "end": v(-3276.6, 0) * mm, "construction": true});
            skLineSegment(sketch, "E216.0", {"start": v(-2286, 3581.86) * mm, "end": v(-2286, 0) * mm, "construction": true});
            skLineSegment(sketch, "E217", {"start": v(762, 1886.99) * mm, "end": v(600.07, 1886.99) * mm, "construction": true});
            skLineSegment(sketch, "E218", {"start": v(600.07, 2133.6) * mm, "end": v(600.07, 3359.15) * mm});
            skLineSegment(sketch, "E219", {"start": v(600.07, 3359.15) * mm, "end": v(-2124.08, 3359.15) * mm});
            skLineSegment(sketch, "E220", {"start": v(-2124.08, 3359.15) * mm, "end": v(-2124.08, 2133.6) * mm});
            skLineSegment(sketch, "E221", {"start": v(-2124.08, 2133.6) * mm, "end": v(600.07, 2133.6) * mm});
            skSolve(sketch);
        }
        {
            var Q0;
            Q0=makeQuery(id+"F19.imprint","IMPRINT",FACE,{"disambiguationData":[TD([[makeQuery(id+"F19.imprint","IMPRINT",EDGE,{"derivedFrom":sQuery(id+"F19.wireOp",EDGE,"E218")}),1.0]])]});
            extrude(context, id + "F20", {"entities" : qUnion([Q0]), "operationType" : NewBodyOperationType.REMOVE, "oppositeDirection" : true, "depth" : 114.3 * mm, "offsetDistance" : 25.4 * mm});
        }
        {
            var Q0;
            Q0=makeQuery(id+"F8.opExtrude","SWEPT_FACE",FACE,{"disambiguationData":[OSD([sQuery(id+"F0.wireOp",EDGE,"E93")])]});
            var sketch = newSketch(context, id + "F21", { "sketchPlane" : qUnion([Q0])});
            skLineSegment(sketch, "E222.0", {"start": v(-3594.1, 0) * mm, "end": v(-1155.7, 0) * mm, "construction": true});
            skLineSegment(sketch, "E223", {"start": v(-1155.7, 0) * mm, "end": v(-1155.7, 914.4) * mm, "construction": true});
            skLineSegment(sketch, "E224", {"start": v(-1155.7, 3413.76) * mm, "end": v(-1155.7, 914.4) * mm});
            skLineSegment(sketch, "E225.0", {"start": v(-2946.4, 3153.3) * mm, "end": v(-2946.4, 0) * mm});
            skLineSegment(sketch, "E226.0", {"start": v(-1155.7, 3413.76) * mm, "end": v(-3594.1, 3059.08) * mm});
            skLineSegment(sketch, "E227", {"start": v(-1155.7, 914.4) * mm, "end": v(-2946.4, 914.4) * mm});
            skSolve(sketch);
        }
        {
            var Q0;
            {var subQ0=sQuery(id+"F21.wireOp",EDGE,"E224");Q0=makeQuery(id+"F21.imprint","IMPRINT",FACE,{"disambiguationData":[TD([[makeQuery(id+"F21.imprint","IMPRINT",EDGE,{"derivedFrom":subQ0}),-1.0]])]});}
            extrude(context, id + "F22", {"entities" : qUnion([Q0]), "operationType" : NewBodyOperationType.REMOVE, "oppositeDirection" : true, "depth" : 114.3 * mm, "offsetDistance" : 25.4 * mm});
        }
        {
            var Q0;
            Q0=qCreatedBy(makeId("Top.planeOp"),FACE);
            var sketch = newSketch(context, id + "F23", { "sketchPlane" : qUnion([Q0])});
            skLineSegment(sketch, "E228.0", {"start": v(-4305.3, 7861.3) * mm, "end": v(-4305.3, -2616.2) * mm});
            skLineSegment(sketch, "E228.1", {"start": v(-4305.3, -2616.2) * mm, "end": v(1181.1, -2616.2) * mm});
            skLineSegment(sketch, "E228.2", {"start": v(6057.9, -2616.2) * mm, "end": v(1181.1, -2616.2) * mm});
            skLineSegment(sketch, "E228.3", {"start": v(6057.9, -2616.2) * mm, "end": v(11544.3, -2616.2) * mm});
            skLineSegment(sketch, "E228.4", {"start": v(11544.3, -2616.2) * mm, "end": v(11544.3, 7861.3) * mm});
            skLineSegment(sketch, "E228.5", {"start": v(11544.3, 7861.3) * mm, "end": v(6362.7, 7861.3) * mm});
            skLineSegment(sketch, "E228.6", {"start": v(6362.7, 7861.3) * mm, "end": v(6362.7, 3708.4) * mm});
            skLineSegment(sketch, "E228.7", {"start": v(876.3, 3730.1) * mm, "end": v(6362.7, 3730.1) * mm});
            skLineSegment(sketch, "E228.8", {"start": v(876.3, 7861.3) * mm, "end": v(876.3, 3708.4) * mm});
            skLineSegment(sketch, "E228.9", {"start": v(876.3, 7861.3) * mm, "end": v(-4305.3, 7861.3) * mm});
            skSolve(sketch);
        }
        {
            var Q0;
            Q0=makeQuery(id+"F23.imprint","IMPRINT",FACE,{"disambiguationData":[TD([[makeQuery(id+"F23.imprint","IMPRINT",EDGE,{"derivedFrom":sQuery(id+"F23.wireOp",EDGE,"E228.0")}),1.0]])]});
            extrude(context, id + "F24", {"entities" : qUnion([Q0]), "oppositeDirection" : true, "depth" : 203.2 * mm, "offsetDistance" : 25.4 * mm});
        }
        {
            var Q0;
            Q0=makeQuery(id+"F24.opExtrude","SWEPT_FACE",FACE,{"disambiguationData":[OSD([sQuery(id+"F23.wireOp",EDGE,"E228.1"),sQuery(id+"F23.wireOp",EDGE,"E228.2"),sQuery(id+"F23.wireOp",EDGE,"E228.3")])]});
            extrude(context, id + "F25", {"entities" : qUnion([Q0]), "depth" : 3048 * mm, "offsetDistance" : 25.4 * mm});
        }
    });
